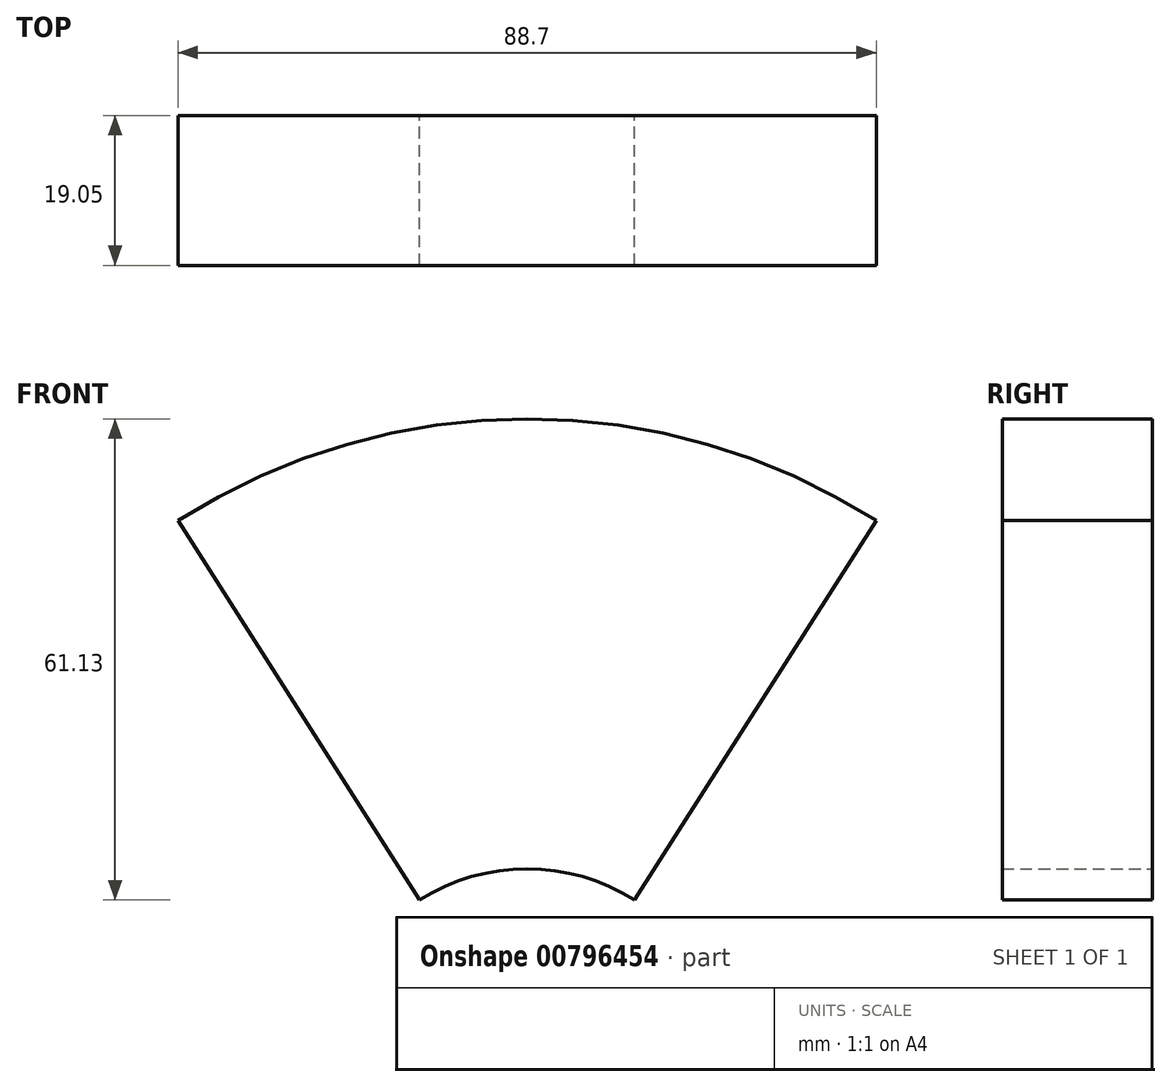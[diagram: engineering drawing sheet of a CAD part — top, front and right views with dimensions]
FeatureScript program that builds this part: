
annotation { "Feature Type Name" : "Feature", "Feature Type Description" : "" }
export const myFeature = defineFeature(function(context is Context, id is Id, definition is map)
    precondition{}
    {
        {
            var Q0;
            Q0=qCreatedBy(makeId("Front.planeOp"),FACE);
            var sketch = newSketch(context, id + "F0", { "sketchPlane" : qUnion([Q0])});
            skArc(sketch, "E0", {"start": v(13.65, 21.42) * mm, "mid": v(0, 25.4) * mm, "end": v(-13.65, 21.42) * mm});
            skArc(sketch, "E1", {"start": v(44.35, 69.62) * mm, "mid": v(0, 82.55) * mm, "end": v(-44.35, 69.62) * mm});
            skLineSegment(sketch, "E2", {"start": v(13.65, 21.42) * mm, "end": v(44.35, 69.62) * mm});
            skLineSegment(sketch, "E3", {"start": v(-13.65, 21.42) * mm, "end": v(-44.35, 69.62) * mm});
            skLineSegment(sketch, "E4", {"start": v(44.35, 69.62) * mm, "end": v(44.35, 0) * mm, "construction": true});
            skLineSegment(sketch, "E5", {"start": v(-44.35, 69.62) * mm, "end": v(-44.35, 0) * mm, "construction": true});
            skSolve(sketch);
        }
        {
            var Q0;
            Q0=makeQuery(id+"F0.imprint","IMPRINT",FACE,{"disambiguationData":[TD([[makeQuery(id+"F0.imprint","IMPRINT",EDGE,{"derivedFrom":sQuery(id+"F0.wireOp",EDGE,"E0")}),-1.0]])]});
            extrude(context, id + "F1", {"entities" : qUnion([Q0]), "depth" : 19.05 * mm, "offsetDistance" : 25.4 * mm});
        }
    });
